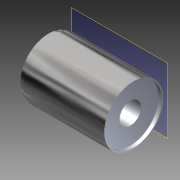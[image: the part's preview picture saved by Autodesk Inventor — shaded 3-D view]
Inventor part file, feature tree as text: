
AUTODESK INVENTOR PART (.ipt)
format: ipt  version: 2015 (Build 190159000, 159)  size: 363,520 bytes
history: native  units: in
note: dims shown in document units (in); Inventor stores cm internally (conversion verified against a paired STEP export)
features: other x3, plane x1, imported_body x1, sketch x1
ambient origin geometry x8: Origin, YZ Plane, XZ Plane, XY Plane, X Axis, Y Axis, Z Axis, Center Point
bodies: Body1 (feature_tree)
feature tree (6):
  other  "18.ipt1"
  plane  "Work Plane1"
  other  "Decal1"
  imported_body  "Base1"
  sketch  "Sketch1"
  other  "Image1"
